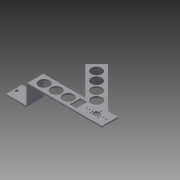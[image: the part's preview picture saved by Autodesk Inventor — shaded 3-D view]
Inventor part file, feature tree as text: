
AUTODESK INVENTOR PART (.ipt)
format: ipt  version: 2013 (Build 170138000, 138)  size: 387,584 bytes
history: native  units: in
note: dims shown in document units (in); Inventor stores cm internally (conversion verified against a paired STEP export)
features: sheet_metal_op x7, other x7, sketch x6
ambient origin geometry x8: Origin, YZ Plane, XZ Plane, XY Plane, X Axis, Y Axis, Z Axis, Center Point
bodies: Solid1 (feature_tree)
feature tree (20):
  sheet_metal_op  "Face1"
  sheet_metal_op  "Flange3"
  sheet_metal_op  "Flange4"
  sketch  "Sketch1"  dims[d5=3.0in]
  other  "Plate1"
  sketch  "Sketch4"  dims[d7=0.75in]
  other  "Plate4"
  sheet_metal_op  "Bend3"
  sheet_metal_op  "Corner3"
  sketch  "Sketch5"  dims[d8=0.125in]
  other  "Plate5"
  sheet_metal_op  "Bend4"
  sheet_metal_op  "Corner4"
  sketch  "Sketch6"  dims[d34=1.5in]
  sketch  "Sketch7"  dims[d35=1.5in]
  sketch  "Sketch8"  dims[d36=0.75in d37=0.75in d39=45.0deg d41=4.0in d42=4.0in d43=0.75in d44=1.25in d45=0.125in d46=0.0625in d47=0.25in d48=0.125in d49=2.0in d50=90.0deg d51=0.05in d52=0.5in d53=0.125in d54=0.125in d55=0.125in d56=0.0625in d57=0.25in d58=0.125in d59=2.0in d60=90.0deg d61=0.05in d62=0.5in d63=0.125in d64=0.125in d65=0.266in d66=0.266in d67=0.25in d68=0.75in d69=0.75in d70=0.25in d71=0.125in d72=0.0in d73=0.266in d74=0.266in d75=0.25in d76=0.75in d77=0.75in d78=0.25in d79=0.125in d80=0.0in d81=1.0in d82=1.0in d83=0.75in d84=0.75in d85=0.75in d86=0.75in d87=1.5748in d89=1.125in d90=0.3937in d92=1.0in d94=1.1811in d96=1.125in d97=0.3937in d99=1.0in d101=0.625in d102=0.625in d103=1.0in d104=0.25in d105=0.125in d106=0.0in d0=1.907in d1=0.125in d2=0.0625in d3=0.25in d4=0.125in d6=0.125in d9=0.125in d10=1.815in d11=0.125in d12=0.0625in d13=0.25in d14=0.125in d15=1.815in d16=0.125in d17=0.0625in d18=0.25in d19=0.125in d20=1.907in d21=0.125in d22=0.0625in d23=0.25in d24=0.125in d26=0.0625in d29=1.815in d30=0.0625in d31=0.25in d32=0.125in d33=0.125in d38=0.125in d40=0.0in]
  other  "Cut1"
  other  "Cut2"
  other  "Cut3"
  other  "Definition1"
